# Revit family: cAssembly-Unico-M_Series-Vertical-Blower+Refrigerant_Coil-Up-Flow
name_source: partatom
category: Mechanical Equipment
units: mm (PartAtom-declared; Revit-internal decimal feet)

## family parameters
Always vertical = Yes
Classification = None
Cut with Voids When Loaded = No
OmniClass Number = 23.75.70.00
OmniClass Title = HVAC Distribution Devices
Part Type = Normal
Room Calculation Point = No
Round Connector Dimension = Use Diameter
Shared = No
Work Plane-Based = No

## types (4) — shared parameters
Alternate Control Box Location = No
Apparent Load = 208 VA
Assembly Code = D3040100
Blower Connection Height = 6 3/8"
Blower Height = 17 1/2"
Blower Width = 13 15/16"
C Drain Pan = 0"
C LUT Blower = Size-Unico
C LUT Heating = Size-V2
C LUT RM = Size-RM
C LUT Return = Size-RC
C LUT VC = Size-VC
C LUT VDC = Size-VDC
C VC Mid Depth = 8 3/4"
Cooling Module Height = 17 1/2"
Default Elevation = 0"
Description = Blower Module
Drain Connection Diameter = 1"
Finish = Metal - Unico - Silver
Frequency = 60 Hz
Instruction Sheet Link = https://www.unicosystem.com
Keynote = 23 30 00
Load Classification = HVAC
Manufacturer = Unico, Inc.
Manufacturer Fax Number = 314-457-9000
Number of Poles = 1
Performance URL = https://www.unicosystem.com
Power Factor = 1
Product Page URL = https://shop.unicosystem.com
Refrigerant Coil Inlet Diameter = 1"
Refrigerant Coil Outlet Diameter = 0"
Return Height = 16 1/4"
Return Module Depth = 17 1/2"
URL = https://www.unicosystem.com
Version = 2020 - v1.0a
Vertical Downlflow Conversion Kit Depth = 7"
Vertical Plenum Module Height = 17 1/2"
Vertical Plenum Module Width = 18 1/4"
Video Link = https://www.youtube.com
Warranty URL = https://www.unicosystem.com

## per-type parameters (varying)
| type | Blower Connection Width | Blower Length | Constraints | Cooling Module Depth | Return Module Height | Return Width | Vertical Conversion Kit Height | Vertical Plenum Module Length |
| M2430 | 6" | 25" | 2 | 13 3/4" | 13 15/16" | 23" | 8" | 25" |
| M3036 | 7 1/4" | 30" | 3 | 13 3/4" | 13 3/4" | 28" | 6" | 30" |
| M3642 | 7 3/16" | 38" | 4 | 13 3/4" | 13 15/16" | 36" | 6" | 38" |
| M4860 | 9 15/16" | 38" | 5 | 18" | 13 15/16" | 36" | 6" | 38" |

note: column(s) folded — value = type name in every type: Model

## geometry (parser evidence)
native form markers: Sweep x17
no freeform markers — native parametric forms only
